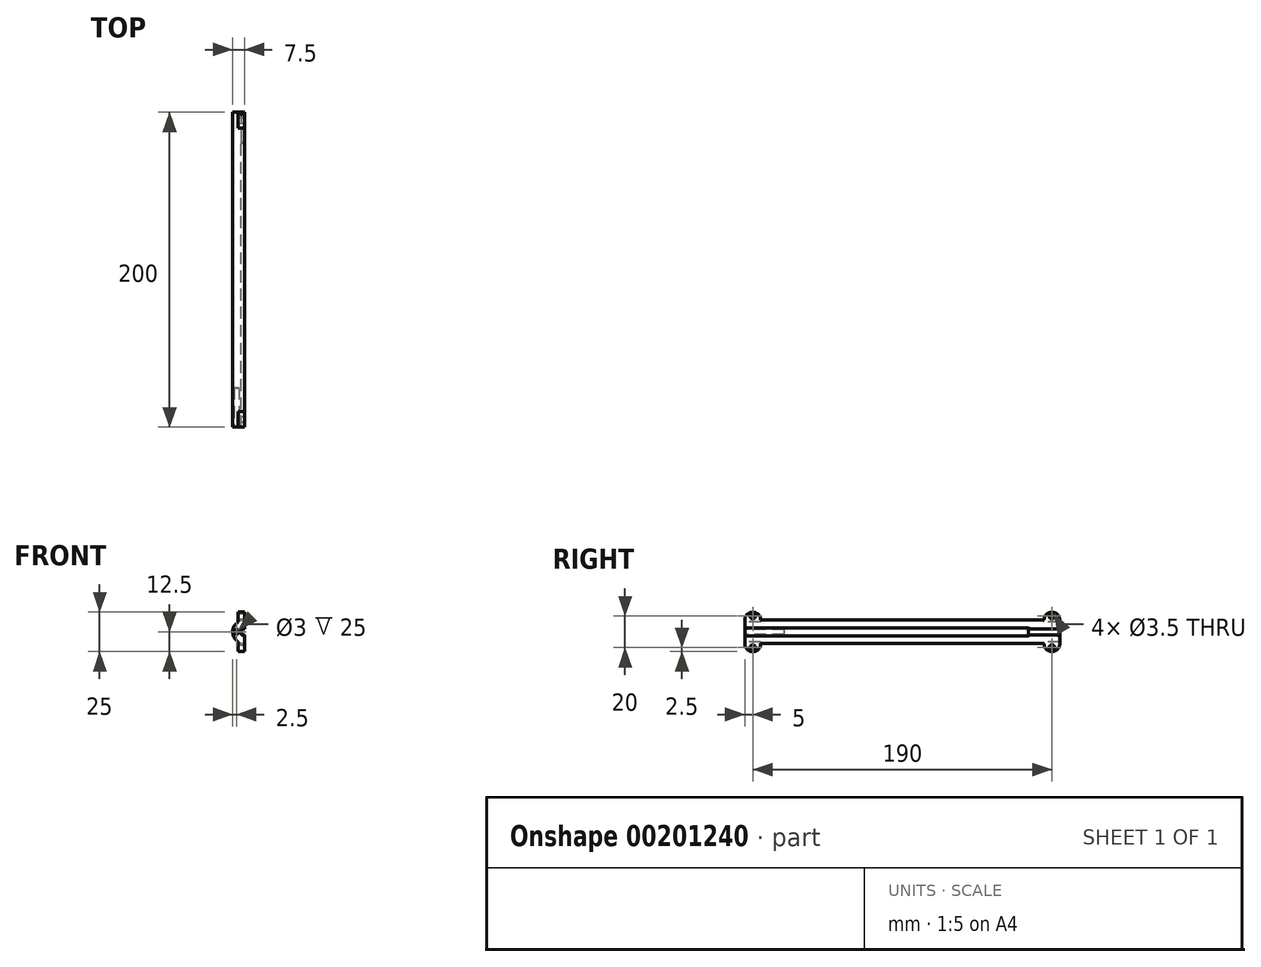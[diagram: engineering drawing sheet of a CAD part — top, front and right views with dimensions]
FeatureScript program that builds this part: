
annotation { "Feature Type Name" : "Feature", "Feature Type Description" : "" }
export const myFeature = defineFeature(function(context is Context, id is Id, definition is map)
    precondition{}
    {
        {
            var Q0;
            Q0=qCreatedBy(makeId("Front.planeOp"),FACE);
            var sketch = newSketch(context, id + "F0", { "sketchPlane" : qUnion([Q0])});
            skCircle(sketch, "E0", {"center": v(0, 0) * mm, "radius": 7.5 * mm});
            skCircle(sketch, "E1", {"center": v(0, 0) * mm, "radius": 2.5 * mm});
            skSolve(sketch);
        }
        {
            var Q0;
            Q0=qSketchRegion(id+"F0",true);
            extrude(context, id + "F1", {"entities" : qUnion([Q0]), "oppositeDirection" : true, "depth" : 200 * mm});
        }
        {
            var Q0;
            Q0=makeQuery(id+"F1.opExtrude","CAP_FACE",FACE,{"disambiguationData":[OSD([sQuery(id+"F0.wireOp",EDGE,"E0"),sQuery(id+"F0.wireOp",EDGE,"E1")])],"isStart":true});
            var sketch = newSketch(context, id + "F2", { "sketchPlane" : qUnion([Q0])});
            skPoint(sketch, "E2", {"position": v(5, 0) * mm});
            skPoint(sketch, "E3", {"position": v(-5, 0) * mm});
            skCircle(sketch, "E4", {"center": v(5, 0) * mm, "radius": 1.5 * mm});
            skCircle(sketch, "E5", {"center": v(-5, 0) * mm, "radius": 1.5 * mm});
            skSolve(sketch);
        }
        {
            var Q0;
            Q0=qSketchRegion(id+"F2",true);
            extrude(context, id + "F3", {"entities" : qUnion([Q0]), "operationType" : NewBodyOperationType.REMOVE, "oppositeDirection" : true, "depth" : 25 * mm});
        }
        {
            var Q0;
            Q0=qCreatedBy(makeId("Right.planeOp"),FACE);
            var sketch = newSketch(context, id + "F4", { "sketchPlane" : qUnion([Q0])});
            skLineSegment(sketch, "E6.bottom", {"start": v(0, 16.4) * mm, "end": v(255.63, 16.4) * mm});
            skLineSegment(sketch, "E6.top", {"start": v(0, -18.35) * mm, "end": v(255.63, -18.35) * mm});
            skLineSegment(sketch, "E6.left", {"start": v(0, 16.4) * mm, "end": v(0, -18.35) * mm});
            skLineSegment(sketch, "E6.right", {"start": v(255.63, 16.4) * mm, "end": v(255.63, -18.35) * mm});
            skSolve(sketch);
        }
        {
            var Q0;
            Q0=qSketchRegion(id+"F4",true);
            extrude(context, id + "F5", {"entities" : qUnion([Q0]), "operationType" : NewBodyOperationType.REMOVE, "depth" : 25 * mm});
        }
        {
            var Q0;
            Q0=makeQuery(id+"F5.boolean.opBoolean","COPY",FACE,{"disambiguationData":[OD(1.0)],"derivedFrom":makeQuery(id+"F5.opExtrude","CAP_FACE",FACE,{"disambiguationData":[OSD([sQuery(id+"F4.wireOp",EDGE,"E6.bottom"),sQuery(id+"F4.wireOp",EDGE,"E6.top"),sQuery(id+"F4.wireOp",EDGE,"E6.left"),sQuery(id+"F4.wireOp",EDGE,"E6.right")])],"isStart":true})});
            var sketch = newSketch(context, id + "F6", { "sketchPlane" : qUnion([Q0])});
            skPoint(sketch, "E7", {"position": v(5, 7.5) * mm});
            skPoint(sketch, "E8", {"position": v(195, 7.5) * mm});
            skArc(sketch, "E9", {"start": v(0, 7.5) * mm, "mid": v(5, 12.5) * mm, "end": v(10, 7.5) * mm});
            skArc(sketch, "E10", {"start": v(200, 7.5) * mm, "mid": v(195, 12.5) * mm, "end": v(190, 7.5) * mm});
            skPoint(sketch, "E11", {"position": v(5, -7.5) * mm});
            skPoint(sketch, "E12", {"position": v(195, -7.5) * mm});
            skArc(sketch, "E13", {"start": v(200, -7.5) * mm, "mid": v(195, -12.5) * mm, "end": v(190, -7.5) * mm});
            skPoint(sketch, "E14", {"position": v(0, -7.5) * mm});
            skPoint(sketch, "E14.positionSnap0", {"position": v(0, 5) * mm});
            skArc(sketch, "E15", {"start": v(0, -7.5) * mm, "mid": v(5, -12.5) * mm, "end": v(10, -7.5) * mm});
            skLineSegment(sketch, "E16.bottom", {"start": v(0, 7.5) * mm, "end": v(10, 7.5) * mm});
            skLineSegment(sketch, "E16.top", {"start": v(0, 2.5) * mm, "end": v(10, 2.5) * mm});
            skLineSegment(sketch, "E16.left", {"start": v(0, 7.5) * mm, "end": v(0, 2.5) * mm});
            skLineSegment(sketch, "E16.right", {"start": v(10, 7.5) * mm, "end": v(10, 2.5) * mm});
            skLineSegment(sketch, "E17.bottom", {"start": v(0, -7.5) * mm, "end": v(10, -7.5) * mm});
            skLineSegment(sketch, "E17.top", {"start": v(0, -2.62) * mm, "end": v(10, -2.62) * mm});
            skLineSegment(sketch, "E17.left", {"start": v(0, -7.5) * mm, "end": v(0, -2.62) * mm});
            skLineSegment(sketch, "E17.right", {"start": v(10, -7.5) * mm, "end": v(10, -2.62) * mm});
            skLineSegment(sketch, "E18.bottom", {"start": v(200, -7.5) * mm, "end": v(190, -7.5) * mm});
            skLineSegment(sketch, "E18.top", {"start": v(200, -2.62) * mm, "end": v(190, -2.62) * mm});
            skLineSegment(sketch, "E18.left", {"start": v(200, -7.5) * mm, "end": v(200, -2.62) * mm});
            skLineSegment(sketch, "E18.right", {"start": v(190, -7.5) * mm, "end": v(190, -2.62) * mm});
            skLineSegment(sketch, "E19.bottom", {"start": v(200, 2.5) * mm, "end": v(190, 2.5) * mm});
            skLineSegment(sketch, "E19.top", {"start": v(200, 7.5) * mm, "end": v(190, 7.5) * mm});
            skLineSegment(sketch, "E19.left", {"start": v(200, 2.5) * mm, "end": v(200, 7.5) * mm});
            skLineSegment(sketch, "E19.right", {"start": v(190, 2.5) * mm, "end": v(190, 7.5) * mm});
            skSolve(sketch);
        }
        {
            var Q0;
            Q0=qSketchRegion(id+"F6",true);
            extrude(context, id + "F7", {"entities" : qUnion([Q0]), "operationType" : NewBodyOperationType.ADD, "oppositeDirection" : true, "depth" : 4 * mm});
        }
        {
            var Q0;
            Q0=makeQuery(id+"F7.boolean.opBoolean","MERGE",FACE,{"derivedFrom":[makeQuery(id+"F5.boolean.opBoolean","COPY",FACE,{"disambiguationData":[OD(1.0)],"derivedFrom":makeQuery(id+"F5.opExtrude","CAP_FACE",FACE,{"disambiguationData":[OSD([sQuery(id+"F4.wireOp",EDGE,"E6.bottom"),sQuery(id+"F4.wireOp",EDGE,"E6.top"),sQuery(id+"F4.wireOp",EDGE,"E6.left"),sQuery(id+"F4.wireOp",EDGE,"E6.right")])],"isStart":true})}),makeQuery(id+"F7.opExtrude","CAP_FACE",FACE,{"disambiguationData":[OSD([sQuery(id+"F6.wireOp",EDGE,"E9"),sQuery(id+"F6.wireOp",EDGE,"E16.top"),sQuery(id+"F6.wireOp",EDGE,"E16.left"),sQuery(id+"F6.wireOp",EDGE,"E16.right")])],"isStart":true}),makeQuery(id+"F7.opExtrude","CAP_FACE",FACE,{"disambiguationData":[OSD([sQuery(id+"F6.wireOp",EDGE,"E10"),sQuery(id+"F6.wireOp",EDGE,"E19.bottom"),sQuery(id+"F6.wireOp",EDGE,"E19.left"),sQuery(id+"F6.wireOp",EDGE,"E19.right")])],"isStart":true})]});
            var sketch = newSketch(context, id + "F8", { "sketchPlane" : qUnion([Q0])});
            skPoint(sketch, "E20", {"position": v(5, 7.5) * mm});
            skPoint(sketch, "E21", {"position": v(195, 7.5) * mm});
            skPoint(sketch, "E22", {"position": v(5, -10) * mm});
            skPoint(sketch, "E23", {"position": v(195, -10) * mm});
            skPoint(sketch, "E24", {"position": v(5, 10) * mm});
            skPoint(sketch, "E25", {"position": v(195, 10) * mm});
            skPoint(sketch, "E26", {"position": v(5, 0) * mm});
            skPoint(sketch, "E27", {"position": v(195, 0) * mm});
            skCircle(sketch, "E28", {"center": v(5, 10) * mm, "radius": 1.75 * mm});
            skCircle(sketch, "E29", {"center": v(5, -10) * mm, "radius": 1.75 * mm});
            skCircle(sketch, "E30", {"center": v(195, 10) * mm, "radius": 1.75 * mm});
            skCircle(sketch, "E31", {"center": v(195, -10) * mm, "radius": 1.75 * mm});
            skSolve(sketch);
        }
        {
            var Q0;
            Q0=qSketchRegion(id+"F8",true);
            extrude(context, id + "F9", {"entities" : qUnion([Q0]), "operationType" : NewBodyOperationType.REMOVE, "endBound" : BoundingType.THROUGH_ALL, "oppositeDirection" : true, "depth" : 25 * mm});
        }
        {
            var Q0;
            Q0=makeQuery(id+"F7.boolean.opBoolean","MERGE",FACE,{"derivedFrom":[makeQuery(id+"F1.opExtrude","CAP_FACE",FACE,{"disambiguationData":[OSD([sQuery(id+"F0.wireOp",EDGE,"E0"),sQuery(id+"F0.wireOp",EDGE,"E1")])],"isStart":false}),makeQuery(id+"F7.opExtrude","SWEPT_FACE",FACE,{"disambiguationData":[OSD([sQuery(id+"F6.wireOp",EDGE,"E18.left")])]}),makeQuery(id+"F7.opExtrude","SWEPT_FACE",FACE,{"disambiguationData":[OSD([sQuery(id+"F6.wireOp",EDGE,"E19.left")])]})]});
            var sketch = newSketch(context, id + "F10", { "sketchPlane" : qUnion([Q0])});
            skPoint(sketch, "E32", {"position": v(0, 0) * mm});
            skArc(sketch, "E33", {"start": v(0, 2) * mm, "mid": v(2, 0) * mm, "end": v(0, -2) * mm});
            skArc(sketch, "E34", {"start": v(0, 2.5) * mm, "mid": v(2.5, 0) * mm, "end": v(0, -2.5) * mm});
            skLineSegment(sketch, "E35", {"start": v(0, 2.5) * mm, "end": v(0, 2) * mm});
            skLineSegment(sketch, "E36", {"start": v(0, -2) * mm, "end": v(0, -2.5) * mm});
            skSolve(sketch);
        }
        {
            var Q0;
            Q0 = qSketchRegion(id + "F10", true);
            extrude(context, id + "F11", {"entities" : qUnion([Q0]), "operationType" : NewBodyOperationType.ADD, "oppositeDirection" : true, "depth" : 20 * mm});
        }
        {
            var Q0;
            Q0=makeQuery(id+"F11.opExtrude","CAP_EDGE",EDGE,{"disambiguationData":[OSD([sQuery(id+"F10.wireOp",EDGE,"E33")])],"isStart":true});
            var Q1;
            Q1=makeQuery(id+"F11.opExtrude","CAP_EDGE",EDGE,{"disambiguationData":[OSD([sQuery(id+"F10.wireOp",EDGE,"E33")])],"isStart":false});
            fillet(context, id + "F12", {"entities" : qUnion([Q0, Q1]), "radius" : 2 * mm, "tangentPropagation" : true, "allowEdgeOverflow" : false});
        }
    });
